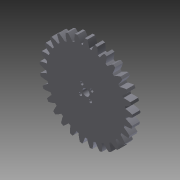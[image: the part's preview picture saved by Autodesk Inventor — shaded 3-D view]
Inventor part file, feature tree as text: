
AUTODESK INVENTOR PART (.ipt)
format: ipt  version: 2015 (Build 190159000, 159)  size: 250,368 bytes
history: native  units: mm (DEFAULTED — no unit token found)
features: plane x3, other x3, sketch x3, extrude x2
ambient origin geometry x8: Origin, YZ Plane, XZ Plane, XY Plane, X Axis, Y Axis, Z Axis, Center Point
bodies: Solid1 (feature_tree)
feature tree (11):
  extrude  "Extrusion1"  Depth=8.89mm TaperAngle=0.0deg
  plane  "Work Plane1"
  plane  "Work Plane2"
  plane  "Work Plane3"
  other  "Spur Gear"
  extrude  "Extrusion2"  Depth=76.2mm TaperAngle=0.0deg
  sketch  "Sketch1"  dims[d0=104.986667mm d1=8.89mm d2=0.0mm]
  sketch  "Sketch2"  dims[d3=98.213333mm d4=76.2mm d5=0.0mm]
  other  "Srf1"
  sketch  "Sketch3"  dims[d6=0.0mm d7=1.083308mm d9=0.0mm d14=0.0mm d15=96.52mm d16=0.0mm d17=0.0mm d18=0.0mm d19=96.52mm d20=25.4mm d21=0.0mm]
  other  "Pitch Diameter"
